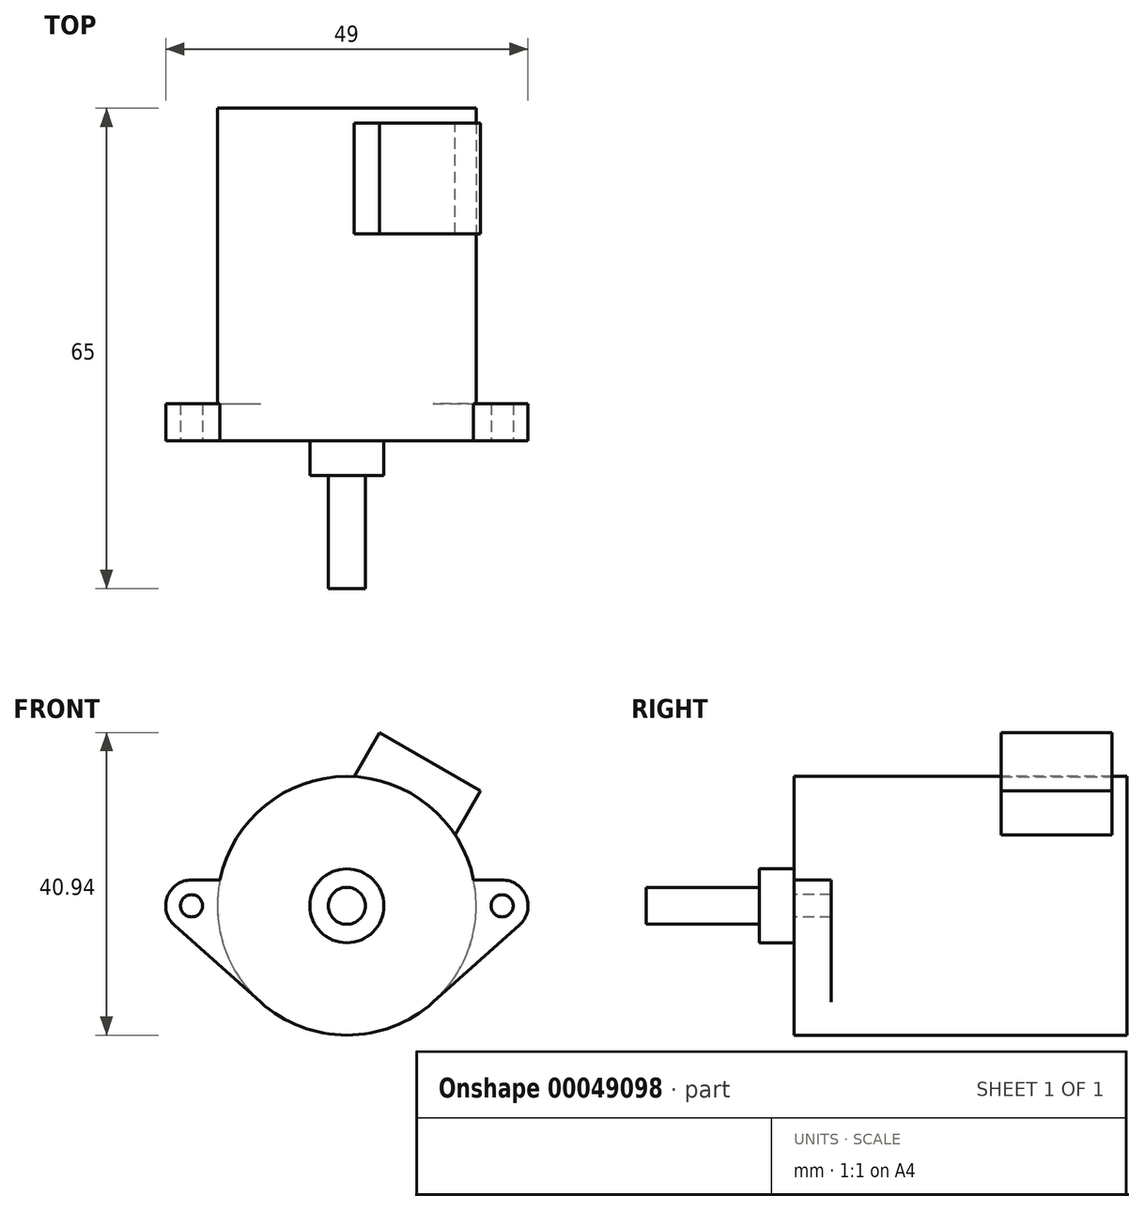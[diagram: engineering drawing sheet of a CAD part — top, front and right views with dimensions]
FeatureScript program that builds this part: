
annotation { "Feature Type Name" : "Feature", "Feature Type Description" : "" }
export const myFeature = defineFeature(function(context is Context, id is Id, definition is map)
    precondition{}
    {
        {
            var Q0;
            Q0=qCreatedBy(makeId("Front.planeOp"),FACE);
            var sketch = newSketch(context, id + "F0", { "sketchPlane" : qUnion([Q0])});
            skArc(sketch, "E0", {"start": v(-11.67, -13.04) * mm, "mid": v(0, -17.5) * mm, "end": v(11.67, -13.04) * mm});
            skLineSegment(sketch, "E1", {"start": v(-36.82, 0) * mm, "end": v(41.01, 0) * mm, "construction": true});
            skCircle(sketch, "E2", {"center": v(-21, 0) * mm, "radius": 1.5 * mm});
            skCircle(sketch, "E3", {"center": v(21, 0) * mm, "radius": 1.5 * mm});
            skLineSegment(sketch, "E4", {"start": v(0, 27.16) * mm, "end": v(0, -31.1) * mm, "construction": true});
            skArc(sketch, "E5", {"start": v(-21, 3.5) * mm, "mid": v(-24.27, 1.25) * mm, "end": v(-23.33, -2.6) * mm});
            skArc(sketch, "E6", {"start": v(23.33, -2.6) * mm, "mid": v(24.27, 1.25) * mm, "end": v(21, 3.5) * mm});
            skLineSegment(sketch, "E7", {"start": v(-21, 3.5) * mm, "end": v(-17.15, 3.5) * mm});
            skLineSegment(sketch, "E8", {"start": v(21, 3.5) * mm, "end": v(17.15, 3.5) * mm});
            skLineSegment(sketch, "E9", {"start": v(23.33, -2.6) * mm, "end": v(11.67, -13.04) * mm});
            skLineSegment(sketch, "E10", {"start": v(-23.33, -2.6) * mm, "end": v(-11.67, -13.04) * mm});
            skArc(sketch, "E11.trimOffspring", {"start": v(17.15, 3.5) * mm, "mid": v(0, 17.5) * mm, "end": v(-17.15, 3.5) * mm});
            skArc(sketch, "E12", {"start": v(17.15, 3.5) * mm, "mid": v(16.61, -5.5) * mm, "end": v(11.67, -13.04) * mm});
            skArc(sketch, "E13", {"start": v(-17.15, 3.5) * mm, "mid": v(-16.61, -5.5) * mm, "end": v(-11.67, -13.04) * mm});
            skCircle(sketch, "E14", {"center": v(0, 0) * mm, "radius": 5 * mm});
            skCircle(sketch, "E15", {"center": v(0, 0) * mm, "radius": 2.5 * mm});
            skSolve(sketch);
        }
        {
            var Q0;
            Q0=makeQuery(id+"F0.imprint","IMPRINT",FACE,{"disambiguationData":[TD([[makeQuery(id+"F0.imprint","IMPRINT",EDGE,{"derivedFrom":sQuery(id+"F0.wireOp",EDGE,"E0")}),1.0]])]});
            var Q1;
            Q1=makeQuery(id+"F0.imprint","IMPRINT",FACE,{"disambiguationData":[TD([[makeQuery(id+"F0.imprint","IMPRINT",EDGE,{"derivedFrom":sQuery(id+"F0.wireOp",EDGE,"E2")}),-1.0]])]});
            var Q2;
            Q2=makeQuery(id+"F0.imprint","IMPRINT",FACE,{"disambiguationData":[TD([[makeQuery(id+"F0.imprint","IMPRINT",EDGE,{"derivedFrom":sQuery(id+"F0.wireOp",EDGE,"E15")}),1.0]])]});
            var Q3;
            Q3=makeQuery(id+"F0.imprint","IMPRINT",FACE,{"disambiguationData":[TD([[makeQuery(id+"F0.imprint","IMPRINT",EDGE,{"derivedFrom":sQuery(id+"F0.wireOp",EDGE,"E3")}),-1.0]])]});
            var Q4;
            Q4=makeQuery(id+"F0.imprint","IMPRINT",FACE,{"disambiguationData":[TD([[makeQuery(id+"F0.imprint","IMPRINT",EDGE,{"derivedFrom":sQuery(id+"F0.wireOp",EDGE,"E14")}),1.0]])]});
            extrude(context, id + "F1", {"entities" : qUnion([Q0, Q1, Q2, Q3, Q4]), "oppositeDirection" : true, "depth" : 5 * mm});
        }
        {
            var Q0;
            Q0=makeQuery(id+"F0.imprint","IMPRINT",FACE,{"disambiguationData":[TD([[makeQuery(id+"F0.imprint","IMPRINT",EDGE,{"derivedFrom":sQuery(id+"F0.wireOp",EDGE,"E0")}),1.0]])]});
            var Q1;
            Q1=makeQuery(id+"F0.imprint","IMPRINT",FACE,{"disambiguationData":[TD([[makeQuery(id+"F0.imprint","IMPRINT",EDGE,{"derivedFrom":sQuery(id+"F0.wireOp",EDGE,"E14")}),1.0]])]});
            var Q2;
            Q2=makeQuery(id+"F0.imprint","IMPRINT",FACE,{"disambiguationData":[TD([[makeQuery(id+"F0.imprint","IMPRINT",EDGE,{"derivedFrom":sQuery(id+"F0.wireOp",EDGE,"E15")}),1.0]])]});
            extrude(context, id + "F2", {"entities" : qUnion([Q0, Q1, Q2]), "operationType" : NewBodyOperationType.ADD, "oppositeDirection" : true, "depth" : 45 * mm});
        }
        {
            var Q0;
            Q0=makeQuery(id+"F0.imprint","IMPRINT",FACE,{"disambiguationData":[TD([[makeQuery(id+"F0.imprint","IMPRINT",EDGE,{"derivedFrom":sQuery(id+"F0.wireOp",EDGE,"E14")}),1.0]])]});
            var Q1;
            Q1=makeQuery(id+"F0.imprint","IMPRINT",FACE,{"disambiguationData":[TD([[makeQuery(id+"F0.imprint","IMPRINT",EDGE,{"derivedFrom":sQuery(id+"F0.wireOp",EDGE,"E15")}),1.0]])]});
            extrude(context, id + "F3", {"entities" : qUnion([Q0, Q1]), "operationType" : NewBodyOperationType.ADD, "depth" : 4.7 * mm});
        }
        {
            var Q0;
            Q0=makeQuery(id+"F0.imprint","IMPRINT",FACE,{"disambiguationData":[TD([[makeQuery(id+"F0.imprint","IMPRINT",EDGE,{"derivedFrom":sQuery(id+"F0.wireOp",EDGE,"E15")}),1.0]])]});
            extrude(context, id + "F4", {"entities" : qUnion([Q0]), "operationType" : NewBodyOperationType.ADD, "depth" : 20 * mm});
        }
        {
            var Q0;
            Q0=makeQuery(id+"F1.opExtrude","SWEPT_BODY",BODY,{"disambiguationData":[OSD([sQuery(id+"F0.wireOp",EDGE,"E0"),sQuery(id+"F0.wireOp",EDGE,"E2"),sQuery(id+"F0.wireOp",EDGE,"E3"),sQuery(id+"F0.wireOp",EDGE,"E5"),sQuery(id+"F0.wireOp",EDGE,"E6"),sQuery(id+"F0.wireOp",EDGE,"E7"),sQuery(id+"F0.wireOp",EDGE,"E8"),sQuery(id+"F0.wireOp",EDGE,"E9"),sQuery(id+"F0.wireOp",EDGE,"E10"),sQuery(id+"F0.wireOp",EDGE,"E11.trimOffspring")])]});
            transform(context, id + "F5", {"entities" : qUnion([Q0]), "transformType" : TransformType.TRANSLATION_3D, "dx" : 0 * mm, "dy" : -43 * mm, "dz" : 0 * mm, "makeCopy" : false});
        }
        {
            var Q0;
            Q0=qCreatedBy(makeId("Front.planeOp"),FACE);
            var sketch = newSketch(context, id + "F6", { "sketchPlane" : qUnion([Q0])});
            skLineSegment(sketch, "E16", {"start": v(4.4, 23.44) * mm, "end": v(18.1, 15.54) * mm});
            skLineSegment(sketch, "E17", {"start": v(18.1, 15.54) * mm, "end": v(14.65, 9.57) * mm});
            skLineSegment(sketch, "E18", {"start": v(14.65, 9.57) * mm, "end": v(0.97, 17.47) * mm});
            skLineSegment(sketch, "E19", {"start": v(0.97, 17.47) * mm, "end": v(4.4, 23.44) * mm});
            skLineSegment(sketch, "E20", {"start": v(0, 0) * mm, "end": v(58.47, 0) * mm, "construction": true});
            skSolve(sketch);
        }
        {
            var Q0;
            Q0 = qSketchRegion(id + "F6", true);
            extrude(context, id + "F7", {"entities" : qUnion([Q0]), "operationType" : NewBodyOperationType.ADD, "depth" : 15 * mm});
        }
    });
